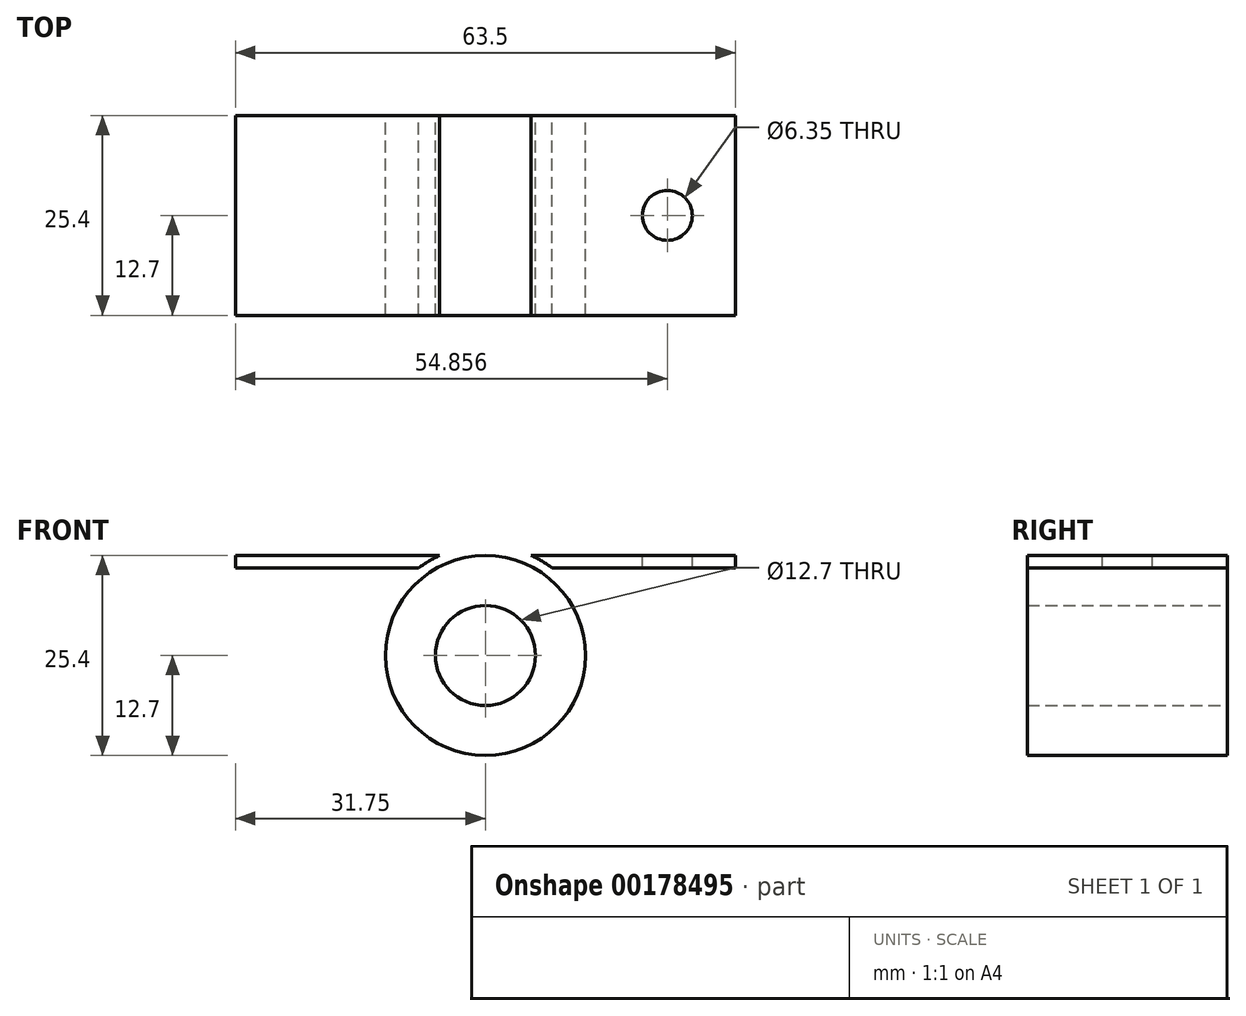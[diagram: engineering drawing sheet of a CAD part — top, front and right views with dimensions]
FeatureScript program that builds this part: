
annotation { "Feature Type Name" : "Feature", "Feature Type Description" : "" }
export const myFeature = defineFeature(function(context is Context, id is Id, definition is map)
    precondition{}
    {
        {
            var Q0;
            Q0=qCreatedBy(makeId("Front.planeOp"),FACE);
            var sketch = newSketch(context, id + "F0", { "sketchPlane" : qUnion([Q0])});
            skCircle(sketch, "E0", {"center": v(0, 0) * mm, "radius": 6.35 * mm});
            skCircle(sketch, "E1", {"center": v(0, 0) * mm, "radius": 12.7 * mm});
            skLineSegment(sketch, "E2", {"start": v(0, 12.7) * mm, "end": v(31.75, 12.7) * mm});
            skLineSegment(sketch, "E3.MirrorCS", {"start": v(0, 12.7) * mm, "end": v(-31.75, 12.7) * mm});
            skLineSegment(sketch, "E4", {"start": v(31.75, 12.7) * mm, "end": v(31.75, 11.11) * mm});
            skLineSegment(sketch, "E5", {"start": v(31.75, 11.11) * mm, "end": v(-31.75, 11.11) * mm});
            skLineSegment(sketch, "E6", {"start": v(-31.75, 11.11) * mm, "end": v(-31.75, 12.7) * mm});
            skCircle(sketch, "E7", {"center": v(0, 0) * mm, "radius": 13.97 * mm});
            skCircle(sketch, "E8", {"center": v(0, 0) * mm, "radius": 14.76 * mm});
            skSolve(sketch);
        }
        {
            var Q0;
            Q0=makeQuery(id+"F0.imprint","IMPRINT",FACE,{"disambiguationData":[TD([[makeQuery(id+"F0.imprint","IMPRINT",EDGE,{"derivedFrom":sQuery(id+"F0.wireOp",EDGE,"E0")}),-1.0]])]});
            var Q1;
            {var subQ0=sQuery(id+"F0.wireOp",EDGE,"E4");Q1=makeQuery(id+"F0.imprint","IMPRINT",FACE,{"disambiguationData":[TD([[makeQuery(id+"F0.imprint","IMPRINT",EDGE,{"derivedFrom":subQ0}),-1.0]])]});}
            var Q2;
            {var subQ0=sQuery(id+"F0.wireOp",EDGE,"E6");Q2=makeQuery(id+"F0.imprint","IMPRINT",FACE,{"disambiguationData":[TD([[makeQuery(id+"F0.imprint","IMPRINT",EDGE,{"derivedFrom":subQ0}),-1.0]])]});}
            var Q3;
            {var subQ3=sQuery(id+"F0.wireOp",EDGE,"E5");var subQ5=sQuery(id+"F0.wireOp",EDGE,"E7");var subQ7=makeQuery(id+"F0.imprint","INTERSECT",VERTEX,{"disambiguationData":[OD(0.0)],"derivedFrom":[subQ3,subQ5]});Q3=makeQuery(id+"F0.imprint","IMPRINT",FACE,{"disambiguationData":[TD([[makeQuery(id+"F0.imprint","IMPRINT",EDGE,{"disambiguationData":[TD([[subQ7,-1.0]])],"derivedFrom":subQ3}),-1.0]])]});}
            var Q4;
            {var subQ0=sQuery(id+"F0.wireOp",EDGE,"E1");var subQ2=sQuery(id+"F0.wireOp",EDGE,"E5");var subQ3=makeQuery(id+"F0.imprint","INTERSECT",VERTEX,{"disambiguationData":[OD(0.0)],"derivedFrom":[subQ0,subQ2]});Q4=makeQuery(id+"F0.imprint","IMPRINT",FACE,{"disambiguationData":[TD([[makeQuery(id+"F0.imprint","IMPRINT",EDGE,{"disambiguationData":[TD([[subQ3,-1.0]])],"derivedFrom":subQ2}),-1.0]])]});}
            var Q5;
            {var subQ3=sQuery(id+"F0.wireOp",EDGE,"E5");var subQ5=sQuery(id+"F0.wireOp",EDGE,"E7");var subQ7=makeQuery(id+"F0.imprint","INTERSECT",VERTEX,{"disambiguationData":[OD(1.0)],"derivedFrom":[subQ3,subQ5]});Q5=makeQuery(id+"F0.imprint","IMPRINT",FACE,{"disambiguationData":[TD([[makeQuery(id+"F0.imprint","IMPRINT",EDGE,{"disambiguationData":[TD([[subQ7,1.0]])],"derivedFrom":subQ3}),-1.0]])]});}
            var Q6;
            {var subQ0=sQuery(id+"F0.wireOp",EDGE,"E8");var subQ1=sQuery(id+"F0.wireOp",EDGE,"E3.MirrorCS");var subQ2=makeQuery(id+"F0.imprint","INTERSECT",VERTEX,{"derivedFrom":[subQ1,subQ0]});Q6=makeQuery(id+"F0.imprint","IMPRINT",FACE,{"disambiguationData":[TD([[makeQuery(id+"F0.imprint","IMPRINT",EDGE,{"disambiguationData":[TD([[subQ2,1.0]])],"derivedFrom":subQ1}),1.0]])]});}
            var Q7;
            {var subQ0=sQuery(id+"F0.wireOp",EDGE,"E8");var subQ1=sQuery(id+"F0.wireOp",EDGE,"E2");var subQ2=makeQuery(id+"F0.imprint","INTERSECT",VERTEX,{"derivedFrom":[subQ1,subQ0]});Q7=makeQuery(id+"F0.imprint","IMPRINT",FACE,{"disambiguationData":[TD([[makeQuery(id+"F0.imprint","IMPRINT",EDGE,{"disambiguationData":[TD([[subQ2,1.0]])],"derivedFrom":subQ1}),-1.0]])]});}
            var Q8;
            {var subQ0=sQuery(id+"F0.wireOp",EDGE,"E8");var subQ1=sQuery(id+"F0.wireOp",EDGE,"E5");var subQ2=makeQuery(id+"F0.imprint","INTERSECT",VERTEX,{"disambiguationData":[OD(0.0)],"derivedFrom":[subQ1,subQ0]});Q8=makeQuery(id+"F0.imprint","IMPRINT",FACE,{"disambiguationData":[TD([[makeQuery(id+"F0.imprint","IMPRINT",EDGE,{"disambiguationData":[TD([[subQ2,-1.0]])],"derivedFrom":subQ1}),1.0]])]});}
            extrude(context, id + "F1", {"entities" : qUnion([Q0, Q1, Q2, Q3, Q4, Q5, Q6, Q7, Q8]), "depth" : 25.4 * mm});
        }
        {
            var Q0;
            Q0=makeQuery(id+"F1.opExtrude","SWEPT_FACE",FACE,{"disambiguationData":[OSD([sQuery(id+"F0.wireOp",EDGE,"E2"),sQuery(id+"F0.wireOp",EDGE,"E3.MirrorCS")])]});
            var sketch = newSketch(context, id + "F2", { "sketchPlane" : qUnion([Q0])});
            skLineSegment(sketch, "E9", {"start": v(-31.75, -12.7) * mm, "end": v(31.75, -12.7) * mm});
            skCircle(sketch, "E10", {"center": v(-21.34, -12.7) * mm, "radius": 3.18 * mm});
            skCircle(sketch, "E11", {"center": v(23.1, -12.7) * mm, "radius": 3.18 * mm});
            skSolve(sketch);
        }
        {
            var Q0;
            {var subQ0=sQuery(id+"F2.wireOp",EDGE,"E10");var subQ1=sQuery(id+"F2.wireOp",EDGE,"E9");var subQ2=makeQuery(id+"F2.imprint","INTERSECT",VERTEX,{"disambiguationData":[OD(0.0)],"derivedFrom":[subQ1,subQ0]});Q0=makeQuery(id+"F2.imprint","IMPRINT",FACE,{"disambiguationData":[TD([[makeQuery(id+"F2.imprint","IMPRINT",EDGE,{"disambiguationData":[TD([[subQ2,-1.0]])],"derivedFrom":subQ1}),-1.0]])]});}
            var Q1;
            {var subQ0=sQuery(id+"F2.wireOp",EDGE,"E10");var subQ1=sQuery(id+"F2.wireOp",EDGE,"E9");var subQ2=makeQuery(id+"F2.imprint","INTERSECT",VERTEX,{"disambiguationData":[OD(0.0)],"derivedFrom":[subQ1,subQ0]});Q1=makeQuery(id+"F2.imprint","IMPRINT",FACE,{"disambiguationData":[TD([[makeQuery(id+"F2.imprint","IMPRINT",EDGE,{"disambiguationData":[TD([[subQ2,-1.0]])],"derivedFrom":subQ1}),1.0]])]});}
            var Q2;
            {var subQ0=sQuery(id+"F2.wireOp",EDGE,"E11");var subQ1=sQuery(id+"F2.wireOp",EDGE,"E9");var subQ2=makeQuery(id+"F2.imprint","INTERSECT",VERTEX,{"disambiguationData":[OD(0.0)],"derivedFrom":[subQ1,subQ0]});Q2=makeQuery(id+"F2.imprint","IMPRINT",FACE,{"disambiguationData":[TD([[makeQuery(id+"F2.imprint","IMPRINT",EDGE,{"disambiguationData":[TD([[subQ2,-1.0]])],"derivedFrom":subQ1}),1.0]])]});}
            var Q3;
            {var subQ0=sQuery(id+"F2.wireOp",EDGE,"E11");var subQ1=sQuery(id+"F2.wireOp",EDGE,"E9");var subQ2=makeQuery(id+"F2.imprint","INTERSECT",VERTEX,{"disambiguationData":[OD(0.0)],"derivedFrom":[subQ1,subQ0]});Q3=makeQuery(id+"F2.imprint","IMPRINT",FACE,{"disambiguationData":[TD([[makeQuery(id+"F2.imprint","IMPRINT",EDGE,{"disambiguationData":[TD([[subQ2,-1.0]])],"derivedFrom":subQ1}),-1.0]])]});}
            extrude(context, id + "F3", {"entities" : qUnion([Q0, Q1, Q2, Q3]), "operationType" : NewBodyOperationType.REMOVE, "oppositeDirection" : true, "depth" : 25.4 * mm});
        }
    });
